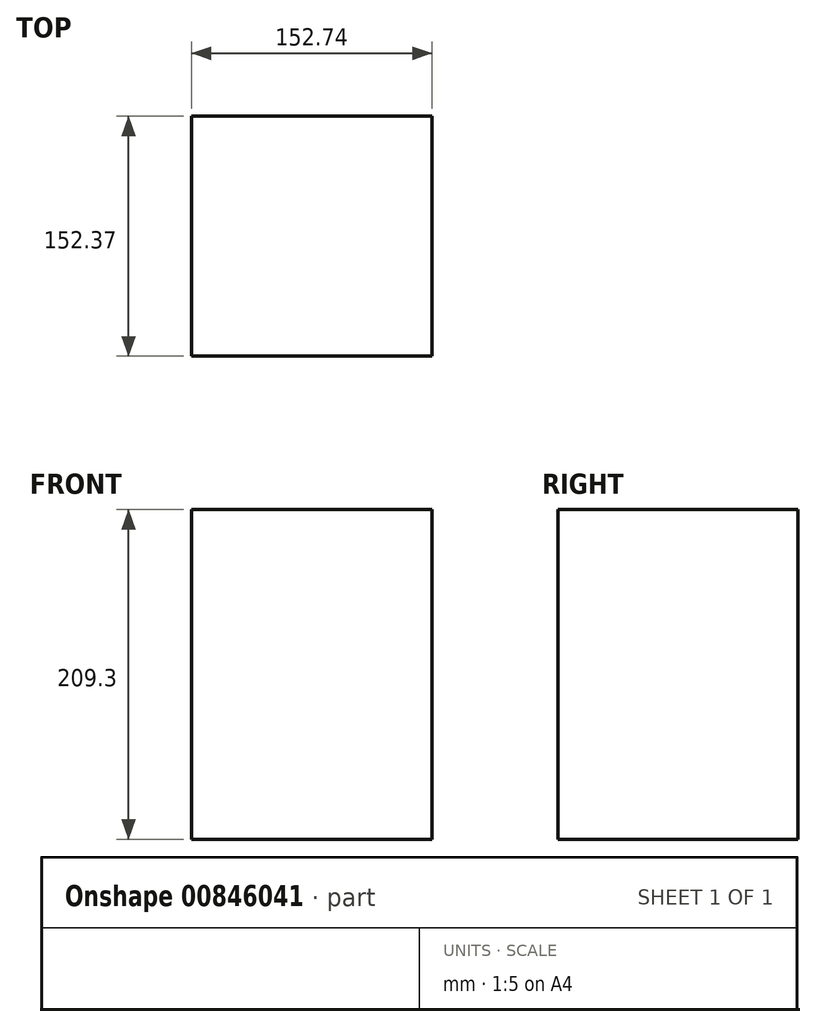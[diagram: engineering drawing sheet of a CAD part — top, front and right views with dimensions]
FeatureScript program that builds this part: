
annotation { "Feature Type Name" : "Feature", "Feature Type Description" : "" }
export const myFeature = defineFeature(function(context is Context, id is Id, definition is map)
    precondition{}
    {
        {
            var Q0;
            Q0=qCreatedBy(makeId("Top.planeOp"),FACE);
            var sketch = newSketch(context, id + "F0", { "sketchPlane" : qUnion([Q0])});
            skLineSegment(sketch, "E0.bottom", {"start": v(-76.37, 76) * mm, "end": v(76.37, 76) * mm});
            skLineSegment(sketch, "E0.top", {"start": v(-76.37, -76.37) * mm, "end": v(76.37, -76.37) * mm});
            skLineSegment(sketch, "E0.left", {"start": v(-76.37, 76) * mm, "end": v(-76.37, -76.37) * mm});
            skLineSegment(sketch, "E0.right", {"start": v(76.37, 76) * mm, "end": v(76.37, -76.37) * mm});
            skSolve(sketch);
        }
        {
            var Q0;
            Q0=makeQuery(id+"F0.imprint","IMPRINT",FACE,{"disambiguationData":[TD([[makeQuery(id+"F0.imprint","IMPRINT",EDGE,{"derivedFrom":sQuery(id+"F0.wireOp",EDGE,"E0.bottom")}),-1.0]])]});
            extrude(context, id + "F1", {"entities" : qUnion([Q0]), "depth" : 209.3 * mm, "offsetDistance" : 25.4 * mm});
        }
    });
